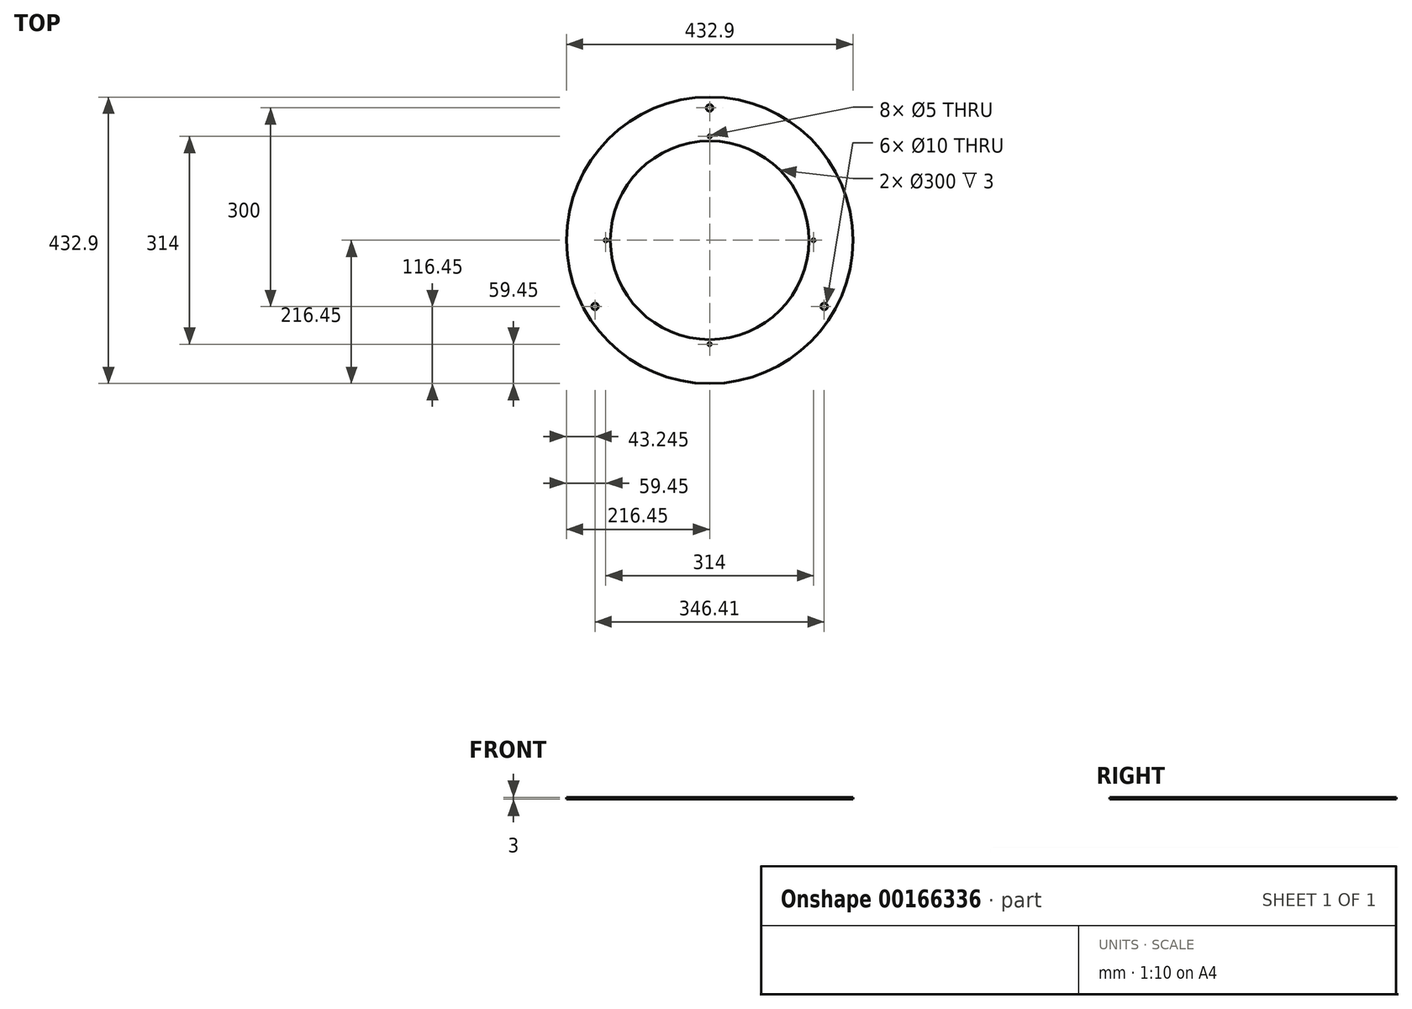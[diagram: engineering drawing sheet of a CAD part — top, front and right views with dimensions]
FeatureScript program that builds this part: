
annotation { "Feature Type Name" : "Feature", "Feature Type Description" : "" }
export const myFeature = defineFeature(function(context is Context, id is Id, definition is map)
    precondition{}
    {
        {
            var Q0;
            Q0=qCreatedBy(makeId("Top.planeOp"),FACE);
            var sketch = newSketch(context, id + "F0", { "sketchPlane" : qUnion([Q0])});
            skCircle(sketch, "E0", {"center": v(0, 0) * mm, "radius": 216.45 * mm});
            skCircle(sketch, "E1", {"center": v(0, 0) * mm, "radius": 150 * mm});
            skSolve(sketch);
        }
        {
            var Q0;
            Q0=makeQuery(id+"F0.imprint","IMPRINT",FACE,{"disambiguationData":[TD([[makeQuery(id+"F0.imprint","IMPRINT",EDGE,{"derivedFrom":sQuery(id+"F0.wireOp",EDGE,"E0")}),1.0]])]});
            extrude(context, id + "F1", {"entities" : qUnion([Q0]), "depth" : 3 * mm});
        }
        {
            var Q0;
            Q0=makeQuery(id+"F1.opExtrude","CAP_FACE",FACE,{"disambiguationData":[OSD([sQuery(id+"F0.wireOp",EDGE,"E0"),sQuery(id+"F0.wireOp",EDGE,"E1")])],"isStart":false});
            var sketch = newSketch(context, id + "F2", { "sketchPlane" : qUnion([Q0])});
            skLineSegment(sketch, "E2", {"start": v(0, 0) * mm, "end": v(0, 200) * mm});
            skCircle(sketch, "E3", {"center": v(0, 200) * mm, "radius": 5 * mm});
            skCircle(sketch, "E4.1.0", {"center": v(-173.2, -100) * mm, "radius": 5 * mm});
            skCircle(sketch, "E4.2.0", {"center": v(173.2, -100) * mm, "radius": 5 * mm});
            skPoint(sketch, "E4.center", {"position": v(0, 0) * mm});
            skSolve(sketch);
        }
        {
            var Q0;
            Q0=qSketchRegion(id+"F2",true);
            extrude(context, id + "F3", {"entities" : qUnion([Q0]), "operationType" : NewBodyOperationType.REMOVE, "oppositeDirection" : true, "depth" : 3 * mm});
        }
        {
            var Q0;
            Q0=makeQuery(id+"F1.opExtrude","CAP_FACE",FACE,{"disambiguationData":[OSD([sQuery(id+"F0.wireOp",EDGE,"E0"),sQuery(id+"F0.wireOp",EDGE,"E1")])],"isStart":false});
            var sketch = newSketch(context, id + "F4", { "sketchPlane" : qUnion([Q0])});
            skLineSegment(sketch, "E5", {"start": v(0, 0) * mm, "end": v(0, 157) * mm});
            skCircle(sketch, "E6", {"center": v(0, 157) * mm, "radius": 2.5 * mm});
            skCircle(sketch, "E7.1.0", {"center": v(-157, 0) * mm, "radius": 2.5 * mm});
            skCircle(sketch, "E7.2.0", {"center": v(0, -157) * mm, "radius": 2.5 * mm});
            skCircle(sketch, "E7.3.0", {"center": v(157, 0) * mm, "radius": 2.5 * mm});
            skPoint(sketch, "E7.center", {"position": v(0, 0) * mm});
            skSolve(sketch);
        }
        {
            var Q0;
            Q0=qSketchRegion(id+"F4",true);
            extrude(context, id + "F5", {"entities" : qUnion([Q0]), "operationType" : NewBodyOperationType.REMOVE, "oppositeDirection" : true, "depth" : 3 * mm});
        }
    });
